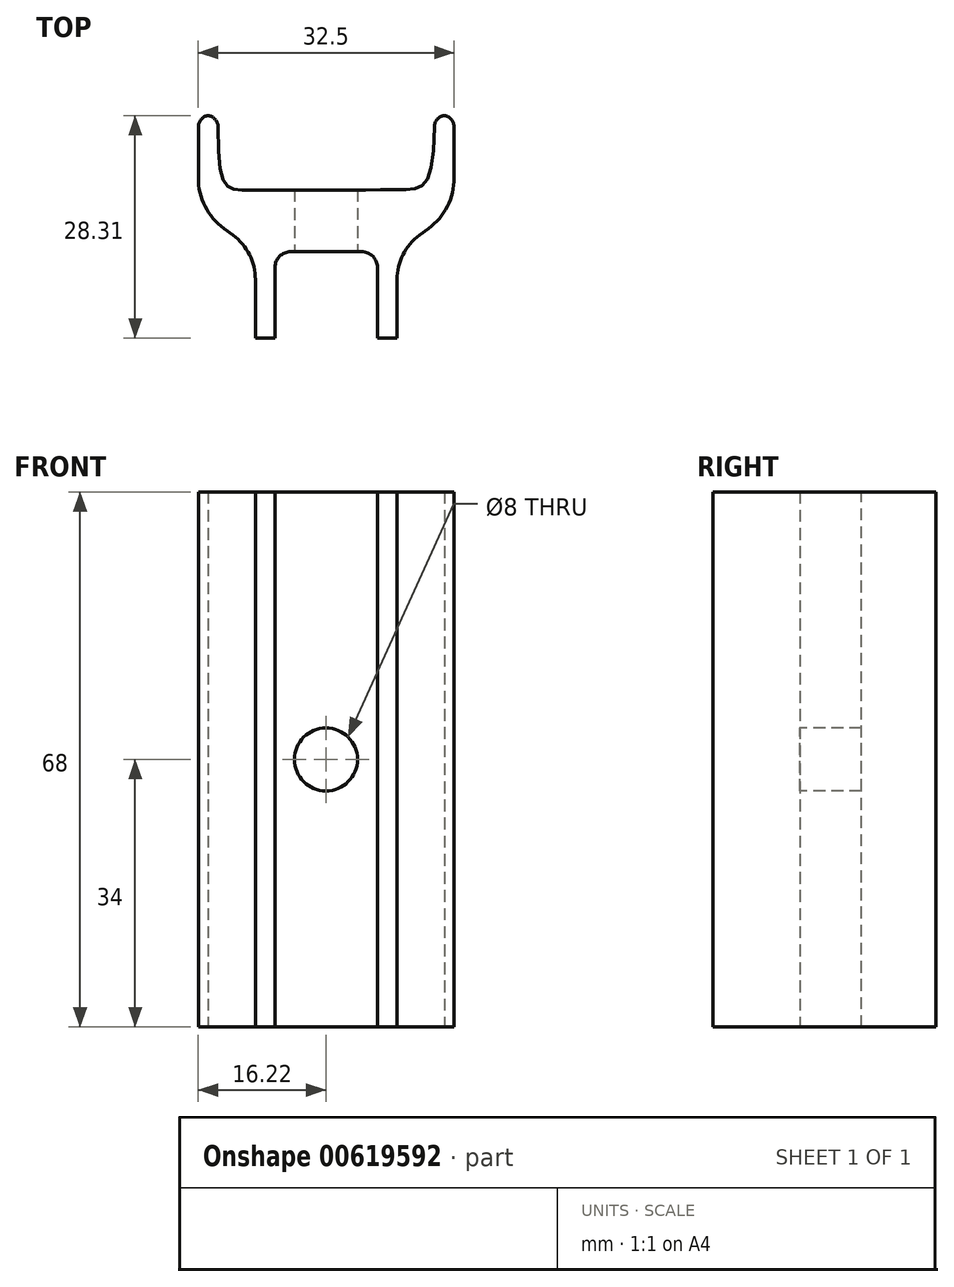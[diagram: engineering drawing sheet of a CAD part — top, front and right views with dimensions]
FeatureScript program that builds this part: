
annotation { "Feature Type Name" : "Feature", "Feature Type Description" : "" }
export const myFeature = defineFeature(function(context is Context, id is Id, definition is map)
    precondition{}
    {
        {
            var Q0;
            Q0=qCreatedBy(makeId("Top.planeOp"),FACE);
            var sketch = newSketch(context, id + "F0", { "sketchPlane" : qUnion([Q0])});
            skPoint(sketch, "E0.middle", {"position": v(0, 0) * mm});
            skLineSegment(sketch, "E1.left", {"start": v(-8.97, 0) * mm, "end": v(-9.8, 7.82) * mm, "construction": true});
            skLineSegment(sketch, "E1.right", {"start": v(9.03, 0) * mm, "end": v(9.03, 7.86) * mm, "construction": true});
            skFitSpline(sketch, "E2", {"points": [v(13.78, 17.33) * mm, v(9.03, 7.86) * mm, v(-9.8, 7.82) * mm, v(-13.72, 17.33) * mm], "startDerivative": vector(0, -94.29) * mm, "endDerivative": vector(0, 96.11) * mm});
            skLineSegment(sketch, "E3", {"start": v(-8.97, 0) * mm, "end": v(-8.97, -11) * mm});
            skLineSegment(sketch, "E4", {"start": v(-8.97, -11) * mm, "end": v(-6.47, -11) * mm});
            skLineSegment(sketch, "E5", {"start": v(9.03, -11) * mm, "end": v(9.03, 0) * mm});
            skLineSegment(sketch, "E6", {"start": v(6.53, -11) * mm, "end": v(6.53, -2) * mm});
            skLineSegment(sketch, "E7", {"start": v(4.53, 0) * mm, "end": v(-4.47, 0) * mm});
            skLineSegment(sketch, "E8", {"start": v(-6.47, -2) * mm, "end": v(-6.47, -11) * mm});
            skLineSegment(sketch, "E9.trimOffspring", {"start": v(6.53, -11) * mm, "end": v(9.03, -11) * mm});
            skArc(sketch, "E10.filletArc", {"start": v(-4.47, 0) * mm, "mid": v(-5.88, -0.59) * mm, "end": v(-6.47, -2) * mm});
            skArc(sketch, "E11.filletArc", {"start": v(6.53, -2) * mm, "mid": v(5.95, -0.59) * mm, "end": v(4.53, 0) * mm});
            skLineSegment(sketch, "E12", {"start": v(-16.22, 5.33) * mm, "end": v(-8.97, 0) * mm});
            skLineSegment(sketch, "E13", {"start": v(0, 0) * mm, "end": v(0, 23.82) * mm, "construction": true});
            skLineSegment(sketch, "E14", {"start": v(9.03, 0) * mm, "end": v(16.28, 5.33) * mm});
            skPoint(sketch, "E15.orphan", {"position": v(9.03, 0) * mm});
            skLineSegment(sketch, "E16", {"start": v(-13.72, 17.33) * mm, "end": v(-16.22, 17.33) * mm});
            skLineSegment(sketch, "E17", {"start": v(-16.22, 17.33) * mm, "end": v(-16.22, 5.33) * mm});
            skLineSegment(sketch, "E18", {"start": v(13.78, 17.33) * mm, "end": v(16.28, 17.33) * mm});
            skLineSegment(sketch, "E19", {"start": v(16.28, 17.33) * mm, "end": v(16.28, 5.33) * mm});
            skPoint(sketch, "E20.orphan", {"position": v(-23.47, 10.67) * mm});
            skPoint(sketch, "E21.orphan", {"position": v(23.53, 10.67) * mm});
            skSolve(sketch);
        }
        {
            var Q0;
            Q0=makeQuery(id+"F0.imprint","IMPRINT",FACE,{"disambiguationData":[TD([[makeQuery(id+"F0.imprint","IMPRINT",EDGE,{"derivedFrom":sQuery(id+"F0.wireOp",EDGE,"E2")}),1.0]])]});
            extrude(context, id + "F1", {"entities" : qUnion([Q0]), "endBound" : BoundingType.SYMMETRIC, "depth" : 68 * mm, "offsetDistance" : 25 * mm});
        }
        {
            var Q0;
            Q0=makeQuery(id+"F1.opExtrude","SWEPT_EDGE",EDGE,{"disambiguationData":[OSD([sQuery(id+"F0.wireOp",EDGE,"E0.top"),sQuery(id+"F0.wireOp",EDGE,"E2"),sQuery(id+"F0.wireOp",EDGE,"E16")])]});
            var Q1;
            Q1=makeQuery(id+"F1.opExtrude","SWEPT_EDGE",EDGE,{"disambiguationData":[OSD([sQuery(id+"F0.wireOp",EDGE,"E16"),sQuery(id+"F0.wireOp",EDGE,"E17")])]});
            var Q2;
            Q2=makeQuery(id+"F1.opExtrude","SWEPT_EDGE",EDGE,{"disambiguationData":[OSD([sQuery(id+"F0.wireOp",EDGE,"E18"),sQuery(id+"F0.wireOp",EDGE,"E19")])]});
            var Q3;
            Q3=makeQuery(id+"F1.opExtrude","SWEPT_EDGE",EDGE,{"disambiguationData":[OSD([sQuery(id+"F0.wireOp",EDGE,"E0.top"),sQuery(id+"F0.wireOp",EDGE,"E2"),sQuery(id+"F0.wireOp",EDGE,"E18")])]});
            fillet(context, id + "F2", {"entities" : qUnion([Q0, Q1, Q2, Q3]), "radius" : 1.5 * mm, "tangentPropagation" : true, "allowEdgeOverflow" : false});
        }
        {
            var Q0;
            Q0=qCreatedBy(makeId("Top.planeOp"),FACE);
            var sketch = newSketch(context, id + "F3", { "sketchPlane" : qUnion([Q0])});
            skFitSpline(sketch, "E22", {"points": [v(26.74, 10.86) * mm, v(16.85, 5.23) * mm, v(0, 5.23) * mm, v(-17.4, 5.69) * mm, v(-26.51, 10.86) * mm], "startDerivative": vector(-62.53, -65.11) * mm, "endDerivative": vector(-26.71, 46.77) * mm});
            skFitSpline(sketch, "E23.0", {"points": [v(24.86, 12.66) * mm, v(24.23, 12) * mm, v(23.1, 10.87) * mm, v(21.72, 9.66) * mm, v(20.62, 8.86) * mm, v(19.75, 8.39) * mm, v(19, 8.12) * mm, v(18.15, 7.94) * mm, v(17.26, 7.86) * mm, v(16.38, 7.8) * mm, v(15.43, 7.77) * mm, v(14.13, 7.74) * mm, v(11.83, 7.72) * mm, v(8.62, 7.75) * mm, v(5.15, 7.8) * mm, v(2.3, 7.83) * mm, v(0.15, 7.84) * mm, v(-1.98, 7.82) * mm, v(-4.76, 7.8) * mm, v(-8.13, 7.76) * mm, v(-11.92, 7.8) * mm, v(-14.82, 7.98) * mm, v(-16.96, 8.24) * mm, v(-18.46, 8.5) * mm, v(-19.8, 8.83) * mm, v(-20.98, 9.26) * mm, v(-22, 9.78) * mm, v(-22.86, 10.4) * mm, v(-23.6, 11.15) * mm, v(-24.05, 11.79) * mm, v(-24.25, 12.15) * mm]});
            skLineSegment(sketch, "E24", {"start": v(-24.23, 12.11) * mm, "end": v(-26.51, 10.86) * mm});
            skLineSegment(sketch, "E25", {"start": v(24.77, 12.56) * mm, "end": v(26.74, 10.86) * mm});
            skSolve(sketch);
        }
        {
            var Q0;
            Q0=makeQuery(id+"F1.opExtrude","SWEPT_FACE",FACE,{"disambiguationData":[OSD([sQuery(id+"F0.wireOp",EDGE,"E7")])]});
            var sketch = newSketch(context, id + "F4", { "sketchPlane" : qUnion([Q0])});
            skPoint(sketch, "E26", {"position": v(0, 0) * mm});
            skSolve(sketch);
        }
        {
            var Q0;
            Q0=sQuery(id+"F4.wireOp",VERTEX,"E26");
            var Q1;
            Q1=makeQuery(id+"F1.opExtrude","SWEPT_BODY",BODY,{"disambiguationData":[OSD([sQuery(id+"F0.wireOp",EDGE,"E2"),sQuery(id+"F0.wireOp",EDGE,"E3"),sQuery(id+"F0.wireOp",EDGE,"E4"),sQuery(id+"F0.wireOp",EDGE,"E5"),sQuery(id+"F0.wireOp",EDGE,"E6"),sQuery(id+"F0.wireOp",EDGE,"E7"),sQuery(id+"F0.wireOp",EDGE,"E8"),sQuery(id+"F0.wireOp",EDGE,"E9.trimOffspring"),sQuery(id+"F0.wireOp",EDGE,"E10.filletArc"),sQuery(id+"F0.wireOp",EDGE,"E11.filletArc"),sQuery(id+"F0.wireOp",EDGE,"E12"),sQuery(id+"F0.wireOp",EDGE,"E14"),sQuery(id+"F0.wireOp",EDGE,"E16"),sQuery(id+"F0.wireOp",EDGE,"E17"),sQuery(id+"F0.wireOp",EDGE,"E18"),sQuery(id+"F0.wireOp",EDGE,"E19")])]});
            hole(context, id + "F5", {"style" : HoleStyle.SIMPLE, "endStyle" : HoleEndStyle.THROUGH, "holeDiameter" : 8 * mm, "majorDiameter" : 5 * mm, "isTappedThrough" : true, "tappedDepth" : 12 * mm, "tapClearance" : 3, "locations" : qUnion([Q0]), "scope" : qUnion([Q1])});
        }
        {
            var Q0;
            Q0=makeQuery(id+"F1.opExtrude","SWEPT_EDGE",EDGE,{"disambiguationData":[OSD([sQuery(id+"F0.wireOp",EDGE,"E12"),sQuery(id+"F0.wireOp",EDGE,"E17")])]});
            var Q1;
            Q1=makeQuery(id+"F1.opExtrude","SWEPT_EDGE",EDGE,{"disambiguationData":[OSD([sQuery(id+"F0.wireOp",EDGE,"E14"),sQuery(id+"F0.wireOp",EDGE,"E19")])]});
            fillet(context, id + "F6", {"entities" : qUnion([Q0, Q1]), "radius" : 8 * mm, "tangentPropagation" : true, "allowEdgeOverflow" : false});
        }
        {
            var Q0;
            Q0=makeQuery(id+"F1.opExtrude","SWEPT_EDGE",EDGE,{"disambiguationData":[OSD([sQuery(id+"F0.wireOp",EDGE,"E5"),sQuery(id+"F0.wireOp",EDGE,"E14")])]});
            var Q1;
            Q1=makeQuery(id+"F1.opExtrude","SWEPT_EDGE",EDGE,{"disambiguationData":[OSD([sQuery(id+"F0.wireOp",EDGE,"E3"),sQuery(id+"F0.wireOp",EDGE,"E12")])]});
            fillet(context, id + "F7", {"entities" : qUnion([Q0, Q1]), "radius" : 7 * mm, "tangentPropagation" : true, "allowEdgeOverflow" : false});
        }
    });
